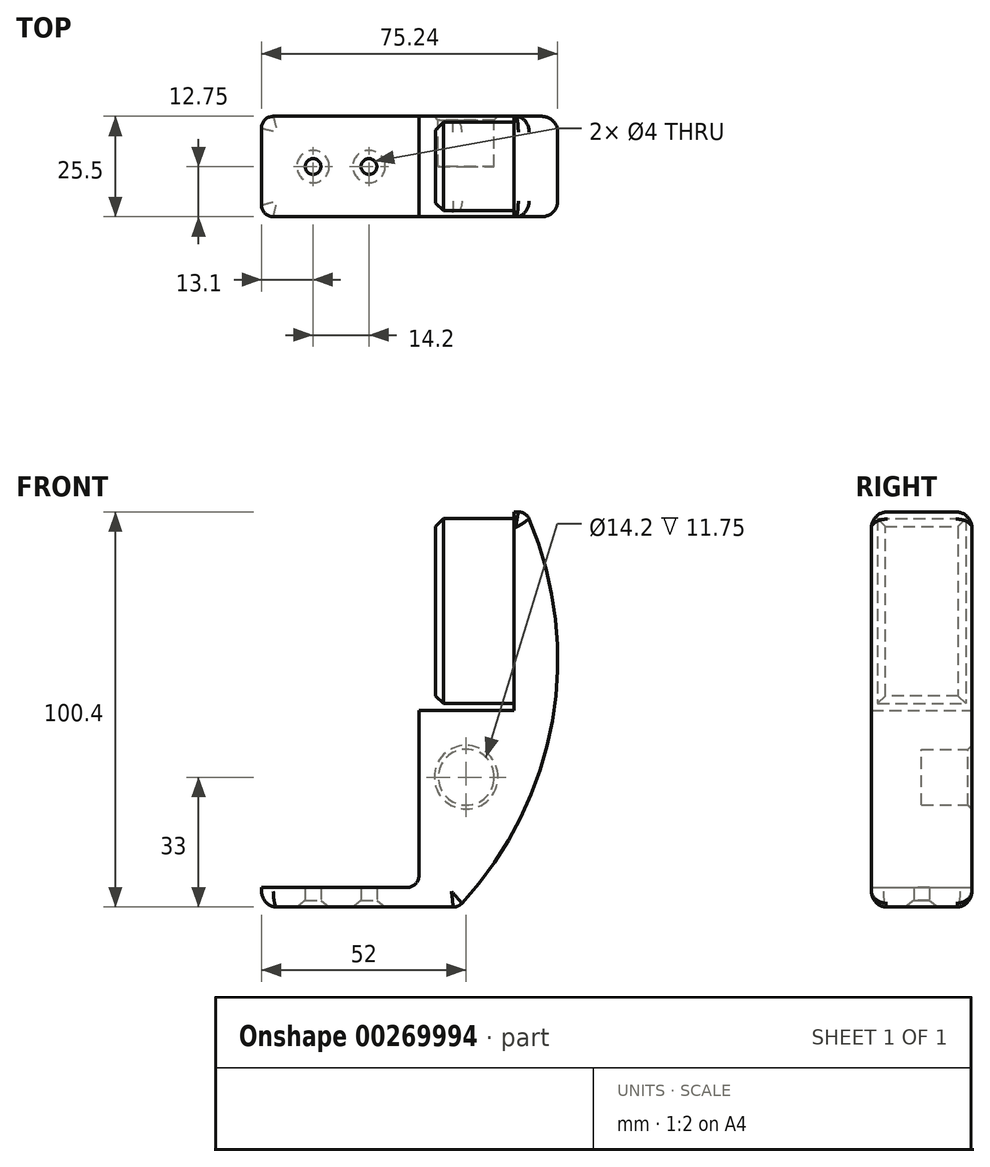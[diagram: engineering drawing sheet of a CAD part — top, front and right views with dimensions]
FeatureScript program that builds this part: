
annotation { "Feature Type Name" : "Feature", "Feature Type Description" : "" }
export const myFeature = defineFeature(function(context is Context, id is Id, definition is map)
    precondition{}
    {
        {
            var Q0;
            Q0=qCreatedBy(makeId("Front.planeOp"),FACE);
            var sketch = newSketch(context, id + "F0", { "sketchPlane" : qUnion([Q0])});
            skLineSegment(sketch, "E0.bottom", {"start": v(0, 0) * mm, "end": v(-40, 0) * mm});
            skLineSegment(sketch, "E0.top", {"start": v(0, 5) * mm, "end": v(-40, 5) * mm});
            skLineSegment(sketch, "E0.right", {"start": v(-40, 0) * mm, "end": v(-40, 5) * mm});
            skLineSegment(sketch, "E1", {"start": v(0, 5) * mm, "end": v(0, 50) * mm});
            skLineSegment(sketch, "E2", {"start": v(0, 50) * mm, "end": v(24.2, 50) * mm});
            skLineSegment(sketch, "E3", {"start": v(24.2, 50) * mm, "end": v(24.2, 51.7) * mm});
            skLineSegment(sketch, "E4", {"start": v(24.2, 51.7) * mm, "end": v(4.2, 51.7) * mm});
            skLineSegment(sketch, "E5", {"start": v(4.2, 51.7) * mm, "end": v(4.2, 98.7) * mm});
            skLineSegment(sketch, "E6", {"start": v(4.2, 98.7) * mm, "end": v(24.2, 98.7) * mm});
            skLineSegment(sketch, "E7", {"start": v(24.2, 98.7) * mm, "end": v(24.2, 100.4) * mm});
            skLineSegment(sketch, "E8", {"start": v(0, 0) * mm, "end": v(10, 0) * mm});
            skArc(sketch, "E9", {"start": v(10, 0) * mm, "mid": v(33.93, 47.57) * mm, "end": v(27.2, 100.4) * mm});
            skLineSegment(sketch, "E10", {"start": v(24.2, 100.4) * mm, "end": v(27.2, 100.4) * mm});
            skLineSegment(sketch, "E11", {"start": v(24.2, 98.7) * mm, "end": v(24.2, 51.7) * mm});
            skCircle(sketch, "E12", {"center": v(12, 33) * mm, "radius": 7.1 * mm});
            skSolve(sketch);
        }
        {
            var Q0;
            Q0=makeQuery(id+"F0.imprint","IMPRINT",FACE,{"disambiguationData":[TD([[makeQuery(id+"F0.imprint","IMPRINT",EDGE,{"derivedFrom":sQuery(id+"F0.wireOp",EDGE,"E0.bottom")}),-1.0]])]});
            extrude(context, id + "F1", {"entities" : qUnion([Q0]), "depth" : 12.75 * mm, "offsetDistance" : 25 * mm, "hasSecondDirection" : true, "secondDirectionOppositeDirection" : true, "secondDirectionDepth" : 12.75 * mm});
        }
        {
            var Q0;
            Q0=makeQuery(id+"F0.imprint","IMPRINT",FACE,{"disambiguationData":[TD([[makeQuery(id+"F0.imprint","IMPRINT",EDGE,{"derivedFrom":sQuery(id+"F0.wireOp",EDGE,"E4")}),-1.0]])]});
            extrude(context, id + "F2", {"entities" : qUnion([Q0]), "operationType" : NewBodyOperationType.ADD, "depth" : 11.25 * mm, "offsetDistance" : 25 * mm, "hasSecondDirection" : true, "secondDirectionOppositeDirection" : true, "secondDirectionDepth" : 11.25 * mm});
        }
        {
            var Q0;
            Q0=makeQuery(id+"F1.opExtrude","SWEPT_EDGE",EDGE,{"disambiguationData":[OSD([sQuery(id+"F0.wireOp",EDGE,"E0.top"),sQuery(id+"F0.wireOp",EDGE,"E1")])]});
            var Q1;
            Q1=makeQuery(id+"F1.opExtrude","CAP_EDGE",EDGE,{"disambiguationData":[OSD([sQuery(id+"F0.wireOp",EDGE,"E0.right")])],"isStart":false});
            var Q2;
            Q2=makeQuery(id+"F1.opExtrude","CAP_EDGE",EDGE,{"disambiguationData":[OSD([sQuery(id+"F0.wireOp",EDGE,"E0.right")])],"isStart":true});
            var Q3;
            Q3=makeQuery(id+"F1.opExtrude","SWEPT_EDGE",EDGE,{"disambiguationData":[OSD([sQuery(id+"F0.wireOp",EDGE,"E8"),sQuery(id+"F0.wireOp",EDGE,"E9")])]});
            var Q4;
            Q4=makeQuery(id+"F1.opExtrude","SWEPT_EDGE",EDGE,{"disambiguationData":[OSD([sQuery(id+"F0.wireOp",EDGE,"E9"),sQuery(id+"F0.wireOp",EDGE,"E10")])]});
            fillet(context, id + "F3", {"entities" : qUnion([Q0, Q1, Q2, Q3, Q4]), "tangentPropagation" : true, "radius" : 3 * mm, "defaultsChanged" : false, "vertexSettings" : [], "allowEdgeOverflow" : false});
        }
        {
            var Q0;
            Q0=makeQuery(id+"F1.opExtrude","CAP_EDGE",EDGE,{"disambiguationData":[OSD([sQuery(id+"F0.wireOp",EDGE,"E9")])],"isStart":true});
            fillet(context, id + "F4", {"entities" : qUnion([Q0]), "tangentPropagation" : true, "radius" : 4 * mm, "defaultsChanged" : true, "vertexSettings" : [], "allowEdgeOverflow" : false});
        }
        {
            var Q0;
            Q0=makeQuery(id+"F1.opExtrude","SWEPT_FACE",FACE,{"disambiguationData":[OSD([sQuery(id+"F0.wireOp",EDGE,"E0.bottom"),sQuery(id+"F0.wireOp",EDGE,"E8")])]});
            var sketch = newSketch(context, id + "F5", { "sketchPlane" : qUnion([Q0])});
            skCircle(sketch, "E13", {"center": v(-26.9, 0) * mm, "radius": 2 * mm});
            skCircle(sketch, "E14", {"center": v(-26.9, 0) * mm, "radius": 4.1 * mm});
            skCircle(sketch, "E15", {"center": v(-12.7, 0) * mm, "radius": 2 * mm});
            skCircle(sketch, "E16", {"center": v(-12.7, 0) * mm, "radius": 4.1 * mm});
            skSolve(sketch);
        }
        {
            var Q0;
            Q0=makeQuery(id+"F5.imprint","IMPRINT",FACE,{"disambiguationData":[TD([[makeQuery(id+"F5.imprint","IMPRINT",EDGE,{"derivedFrom":sQuery(id+"F5.wireOp",EDGE,"E15")}),1.0]])]});
            var Q1;
            Q1=makeQuery(id+"F5.imprint","IMPRINT",FACE,{"disambiguationData":[TD([[makeQuery(id+"F5.imprint","IMPRINT",EDGE,{"derivedFrom":sQuery(id+"F5.wireOp",EDGE,"E13")}),1.0]])]});
            var Q2;
            Q2=makeQuery(id+"F1.opExtrude","SWEPT_FACE",FACE,{"disambiguationData":[OSD([sQuery(id+"F0.wireOp",EDGE,"E0.top")])]});
            extrude(context, id + "F6", {"entities" : qUnion([Q0, Q1]), "operationType" : NewBodyOperationType.REMOVE, "endBound" : BoundingType.UP_TO_SURFACE, "oppositeDirection" : true, "depth" : 25 * mm, "endBoundEntityFace" : qUnion([Q2]), "offsetDistance" : 25 * mm});
        }
        {
            var Q0;
            Q0=makeQuery(id+"F5.imprint","IMPRINT",FACE,{"disambiguationData":[TD([[makeQuery(id+"F5.imprint","IMPRINT",EDGE,{"derivedFrom":sQuery(id+"F5.wireOp",EDGE,"E15")}),-1.0]])]});
            var Q1;
            Q1=makeQuery(id+"F5.imprint","IMPRINT",FACE,{"disambiguationData":[TD([[makeQuery(id+"F5.imprint","IMPRINT",EDGE,{"derivedFrom":sQuery(id+"F5.wireOp",EDGE,"E15")}),1.0]])]});
            var Q2;
            Q2=makeQuery(id+"F5.imprint","IMPRINT",FACE,{"disambiguationData":[TD([[makeQuery(id+"F5.imprint","IMPRINT",EDGE,{"derivedFrom":sQuery(id+"F5.wireOp",EDGE,"E13")}),-1.0]])]});
            var Q3;
            Q3=makeQuery(id+"F5.imprint","IMPRINT",FACE,{"disambiguationData":[TD([[makeQuery(id+"F5.imprint","IMPRINT",EDGE,{"derivedFrom":sQuery(id+"F5.wireOp",EDGE,"E13")}),1.0]])]});
            extrude(context, id + "F7", {"entities" : qUnion([Q0, Q1, Q2, Q3]), "operationType" : NewBodyOperationType.REMOVE, "oppositeDirection" : true, "depth" : 3 * mm, "offsetDistance" : 25 * mm, "hasDraft" : true, "draftAngle" : 50 * degree, "draftPullDirection" : true});
        }
        {
            var Q0;
            Q0=makeQuery(id+"F0.imprint","IMPRINT",FACE,{"disambiguationData":[TD([[makeQuery(id+"F0.imprint","IMPRINT",EDGE,{"derivedFrom":sQuery(id+"F0.wireOp",EDGE,"E12")}),1.0]])]});
            var Q1;
            Q1=makeQuery(id+"F1.opExtrude","CAP_FACE",FACE,{"disambiguationData":[OSD([sQuery(id+"F0.wireOp",EDGE,"E0.bottom"),sQuery(id+"F0.wireOp",EDGE,"E0.top"),sQuery(id+"F0.wireOp",EDGE,"E0.right"),sQuery(id+"F0.wireOp",EDGE,"E1"),sQuery(id+"F0.wireOp",EDGE,"E2"),sQuery(id+"F0.wireOp",EDGE,"E3"),sQuery(id+"F0.wireOp",EDGE,"E7"),sQuery(id+"F0.wireOp",EDGE,"E8"),sQuery(id+"F0.wireOp",EDGE,"E9"),sQuery(id+"F0.wireOp",EDGE,"E10"),sQuery(id+"F0.wireOp",EDGE,"E11"),sQuery(id+"F0.wireOp",EDGE,"E12")])],"isStart":false});
            extrude(context, id + "F8", {"entities" : qUnion([Q0]), "operationType" : NewBodyOperationType.ADD, "endBound" : BoundingType.UP_TO_SURFACE, "depth" : 25 * mm, "endBoundEntityFace" : qUnion([Q1]), "offsetDistance" : 25 * mm});
        }
        {
            var Q0;
            Q0=makeQuery(id+"F1.opExtrude","CAP_EDGE",EDGE,{"disambiguationData":[OSD([sQuery(id+"F0.wireOp",EDGE,"E12")])],"isStart":true});
            chamfer(context, id + "F9", {"entities" : qUnion([Q0]), "width" : 1 * mm, "tangentPropagation" : true});
        }
        {
            var Q0;
            Q0=makeQuery(id+"F2.opExtrude","SWEPT_EDGE",EDGE,{"disambiguationData":[OSD([sQuery(id+"F0.wireOp",EDGE,"E5"),sQuery(id+"F0.wireOp",EDGE,"E6")])]});
            var Q1;
            Q1=makeQuery(id+"F2.opExtrude","CAP_EDGE",EDGE,{"disambiguationData":[OSD([sQuery(id+"F0.wireOp",EDGE,"E5")])],"isStart":false});
            var Q2;
            Q2=makeQuery(id+"F2.opExtrude","CAP_EDGE",EDGE,{"disambiguationData":[OSD([sQuery(id+"F0.wireOp",EDGE,"E5")])],"isStart":true});
            var Q3;
            Q3=makeQuery(id+"F2.opExtrude","SWEPT_EDGE",EDGE,{"disambiguationData":[OSD([sQuery(id+"F0.wireOp",EDGE,"E4"),sQuery(id+"F0.wireOp",EDGE,"E5")])]});
            chamfer(context, id + "F10", {"entities" : qUnion([Q0, Q1, Q2, Q3]), "width" : 2 * mm, "tangentPropagation" : true});
        }
    });
